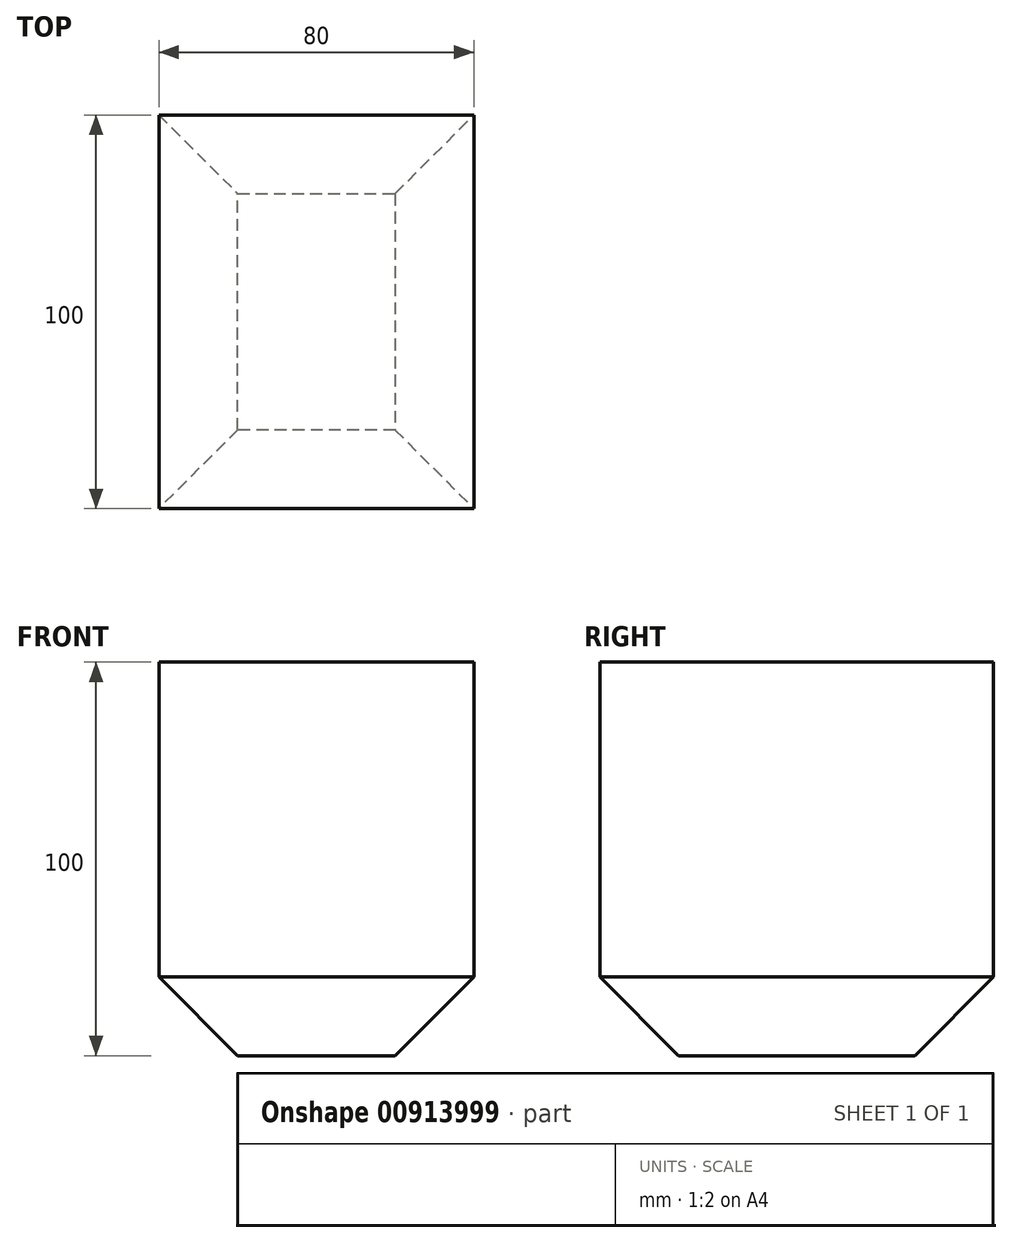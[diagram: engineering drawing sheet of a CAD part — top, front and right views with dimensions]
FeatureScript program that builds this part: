
annotation { "Feature Type Name" : "Feature", "Feature Type Description" : "" }
export const myFeature = defineFeature(function(context is Context, id is Id, definition is map)
    precondition{}
    {
        {
            var Q0;
            Q0=qCreatedBy(makeId("Top.planeOp"),FACE);
            var sketch = newSketch(context, id + "F0", { "sketchPlane" : qUnion([Q0])});
            skLineSegment(sketch, "E0.bottom", {"start": v(0, 0) * mm, "end": v(80, 0) * mm});
            skLineSegment(sketch, "E0.top", {"start": v(0, -100) * mm, "end": v(80, -100) * mm});
            skLineSegment(sketch, "E0.left", {"start": v(0, 0) * mm, "end": v(0, -100) * mm});
            skLineSegment(sketch, "E0.right", {"start": v(80, 0) * mm, "end": v(80, -100) * mm});
            skSolve(sketch);
        }
        {
            var Q0;
            Q0=makeQuery(id+"F0.imprint","IMPRINT",FACE,{"disambiguationData":[TD([[makeQuery(id+"F0.imprint","IMPRINT",EDGE,{"derivedFrom":sQuery(id+"F0.wireOp",EDGE,"E0.bottom")}),-1.0]])]});
            extrude(context, id + "F1", {"entities" : qUnion([Q0]), "oppositeDirection" : true, "depth" : 100 * mm, "offsetDistance" : 25 * mm});
        }
        {
            var Q0;
            Q0=makeQuery(id+"F1.opExtrude","CAP_EDGE",EDGE,{"disambiguationData":[OSD([sQuery(id+"F0.wireOp",EDGE,"E0.right")])],"isStart":false});
            var Q1;
            Q1=makeQuery(id+"F1.opExtrude","CAP_EDGE",EDGE,{"disambiguationData":[OSD([sQuery(id+"F0.wireOp",EDGE,"E0.top")])],"isStart":false});
            var Q2;
            Q2=makeQuery(id+"F1.opExtrude","CAP_EDGE",EDGE,{"disambiguationData":[OSD([sQuery(id+"F0.wireOp",EDGE,"E0.bottom")])],"isStart":false});
            var Q3;
            Q3=makeQuery(id+"F1.opExtrude","CAP_EDGE",EDGE,{"disambiguationData":[OSD([sQuery(id+"F0.wireOp",EDGE,"E0.left")])],"isStart":false});
            chamfer(context, id + "F2", {"entities" : qUnion([Q0, Q1, Q2, Q3]), "width" : 20 * mm, "tangentPropagation" : true});
        }
    });
